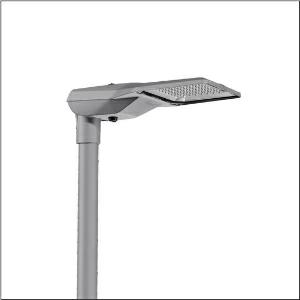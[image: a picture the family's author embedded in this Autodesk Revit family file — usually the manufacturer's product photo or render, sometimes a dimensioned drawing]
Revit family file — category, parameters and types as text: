
# Revit family: streetlight_sl_21_iq_midi___st0_8a_5xe3c31y08nb_292d
name_source: partatom
category: Lighting Fixtures
units: mm (PartAtom-declared; Revit-internal decimal feet)

## family parameters
Cut with Voids When Loaded = No
Host = Face
Light Source = No
Part Type = Normal
Room Calculation Point = No
Round Connector Dimension = Use Diameter
Shared = No

## types (1)
- --- (1 x LED, 21550 lm, 136.6 W, 3000K)
    Apparent Load = 137 VA
    CIE Flux Codes = 41 75 97 100 100
    Color Rendering = 70
    Color Temperature = 3000K
    Default Elevation = 1800 mm
    Description = Streetlight SL 21 iQ midi, mast luminaire, primary light control with lens, of PMMA, primary optical cover: cover, of toughened safety glass, transparent, light distribution: ST0.8a, light emission: direct distribution, primary light characteristic: asymmetric, installation type: post-top, side-entry, LED, High Power LED, rated luminous flux: 21.550lm, luminous efficacy: 158lm/W, light colour: 730, colour temperature: 3000K, control: presetting dimming logarithmic, Street-Remote, Auto-Match, Temp-Guard, Lumen-Switch, Night-Set, Smart-Wire, Light-Fading, Desk-Remote (wireless, voltage-free reading and setting of iQ features in the workshop via application-optimized NFC function/RFID function), optimised constant luminous flux control (CLO 2.0), mains connection: 230..240V, AC, 50/60Hz, start of lifetime: 137W, end of service life: 144W, reduction: 61W, luminaire housing, of diecast aluminium, powder-coated, Siteco® metallic grey (DB 702S), corrosivity category C5 mid according to DIN EN ISO 12944, please order mast flange separately, inclination adjustable: 0°, 5°, 10°, 15°, sealing non-destructively replaceable, multi-level sealing system, length: 644mm, width: 335mm, height: 110mm, mast flange for spigot size: 42mm (side-entry): 5XC10008XM4, 60/48mm (side-entry/post-top): 5XC10108XM2, 76/60mm (side-entry/post-top): 5XC10108XM1, Smart Interface below and above, protection rating (complete): IP66, insulation class (complete): insulation class II (safety insulation), certification: CE, ENEC, ENEC+, VDE, impact resistance: IK09, permissible operating ambient temperature for outdoor applications: -40..+50°C, standard-compliant lighting for roads and squares, packaging unit: 1 piece

Light Distribution: ST0.8a
    Height = 111 mm
    Lamp = 1 x LED
    Lamp Light Flux = 21550 lm
    Lamp Power = 136.6 W
    Lamp count = 1
    Length = 644 mm
    Luminous efficacy = 158 lm/W
    Manufacturer = Siteco
    ModVariant = No
    Model = 5XE3C31Y08NB
    Number of Poles = 1
    OnlyDefault = Yes
    Power Factor = 1
    Product Name = Streetlight SL 21 iQ midi | ST0.8a
    Product group = mast luminaire | pylon top
    ProductGroupID = 6100
    Protection Class = Protection class II
    Protection Degree = IP 66
    RLX_Detail_Level = 1
    RLX_Emergency_Light_Flux = 0 lm
    RLX_Emergency_Type = 0
    RLX_Emergency_Type_DB = No
    RlxData = <blob elided: 92293 chars, md5=75d5b7ee>
    Socket = socket
    Standby Power = 0 W
    System Light Flux = 21550 lm
    System Power = 137 W
    Type Comments = factory setting: luminous flux: 100 % | dim-lin: 254 | 733 mA
    Type Image = l_1004304.jpg
    URL = http://relux.com
    VarID = @adj_043233
    Voltage = 0 V
    Weight = 0.00 kg
    Width = 336 mm

## geometry (parser evidence)
native form markers: Blend x4, Sweep x12
no freeform markers — native parametric forms only
